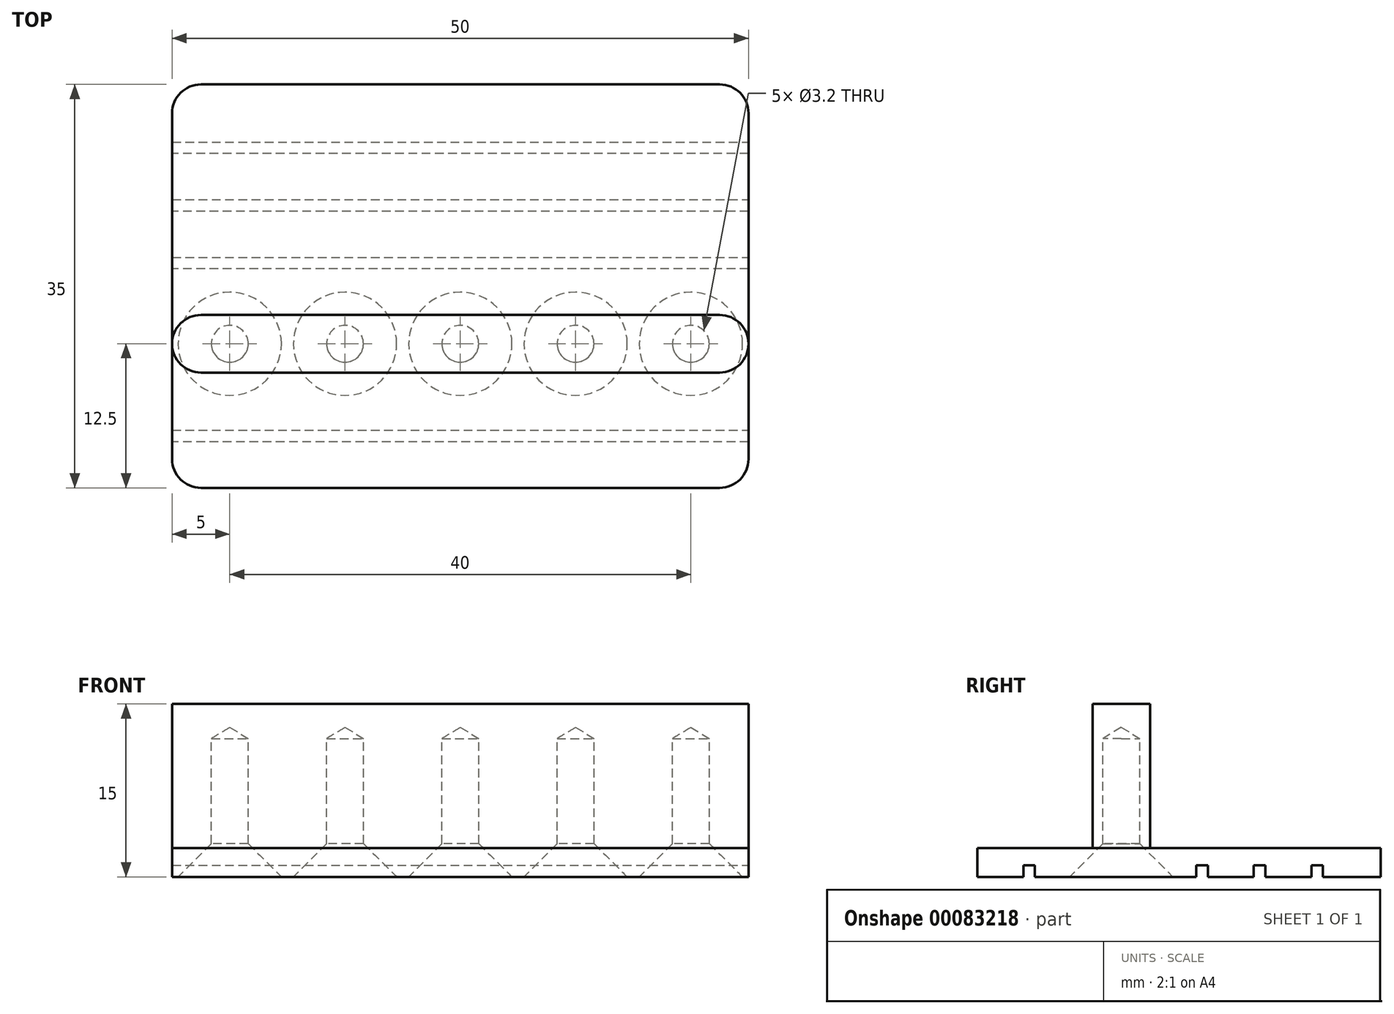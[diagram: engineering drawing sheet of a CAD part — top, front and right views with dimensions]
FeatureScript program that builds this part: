
annotation { "Feature Type Name" : "Feature", "Feature Type Description" : "" }
export const myFeature = defineFeature(function(context is Context, id is Id, definition is map)
    precondition{}
    {
        {
            var Q0;
            Q0=qCreatedBy(makeId("Top.planeOp"),FACE);
            var sketch = newSketch(context, id + "F0", { "sketchPlane" : qUnion([Q0])});
            skLineSegment(sketch, "E0.bottom", {"start": v(25, 17.5) * mm, "end": v(-25, 17.5) * mm});
            skLineSegment(sketch, "E0.top", {"start": v(25, -17.5) * mm, "end": v(-25, -17.5) * mm});
            skLineSegment(sketch, "E0.left", {"start": v(25, 17.5) * mm, "end": v(25, -17.5) * mm});
            skLineSegment(sketch, "E0.right", {"start": v(-25, 17.5) * mm, "end": v(-25, -17.5) * mm});
            skPoint(sketch, "E0.middle", {"position": v(0, 0) * mm});
            skLineSegment(sketch, "E1", {"start": v(-25, -7.5) * mm, "end": v(25, -7.5) * mm});
            skLineSegment(sketch, "E2", {"start": v(25, -7.5) * mm, "end": v(25, -2.5) * mm});
            skLineSegment(sketch, "E3", {"start": v(25, -2.5) * mm, "end": v(-25, -2.5) * mm});
            skLineSegment(sketch, "E4", {"start": v(-25, -5) * mm, "end": v(25, -5) * mm, "construction": true});
            skPoint(sketch, "E5", {"position": v(0, -5) * mm});
            skPoint(sketch, "E6", {"position": v(20, -5) * mm});
            skPoint(sketch, "E7", {"position": v(-20, -5) * mm});
            skPoint(sketch, "E8", {"position": v(-10, -5) * mm});
            skPoint(sketch, "E9", {"position": v(10, -5) * mm});
            skLineSegment(sketch, "E10", {"start": v(-25, 12.5) * mm, "end": v(25, 12.5) * mm});
            skLineSegment(sketch, "E11", {"start": v(25, 12.5) * mm, "end": v(25, 11.5) * mm});
            skLineSegment(sketch, "E12", {"start": v(25, 11.5) * mm, "end": v(-25, 11.5) * mm});
            skLineSegment(sketch, "E13.0.1.0", {"start": v(25, 6.5) * mm, "end": v(-25, 6.5) * mm});
            skLineSegment(sketch, "E13.0.1.1", {"start": v(-25, 7.5) * mm, "end": v(25, 7.5) * mm});
            skLineSegment(sketch, "E13.0.2.0", {"start": v(25, 1.5) * mm, "end": v(-25, 1.5) * mm});
            skLineSegment(sketch, "E13.0.2.1", {"start": v(-25, 2.5) * mm, "end": v(25, 2.5) * mm});
            skLineSegment(sketch, "E13.0.3.0", {"start": v(25, -3.5) * mm, "end": v(-25, -3.5) * mm});
            skLineSegment(sketch, "E13.0.3.1", {"start": v(-25, -2.5) * mm, "end": v(25, -2.5) * mm});
            skLineSegment(sketch, "E13.0.4.0", {"start": v(25, -8.5) * mm, "end": v(-25, -8.5) * mm});
            skLineSegment(sketch, "E13.0.5.0", {"start": v(25, -13.5) * mm, "end": v(-25, -13.5) * mm});
            skLineSegment(sketch, "E13.0.5.1", {"start": v(-25, -12.5) * mm, "end": v(25, -12.5) * mm});
            skLineSegment(sketch, "E13.direction1", {"start": v(-25, 11.5) * mm, "end": v(0, 11.5) * mm, "construction": true});
            skLineSegment(sketch, "E13.direction2", {"start": v(-25, 11.5) * mm, "end": v(-25, 6.5) * mm, "construction": true});
            skSolve(sketch);
        }
        {
            var Q0;
            {var subQ0=sQuery(id+"F0.wireOp",EDGE,"E0.bottom");Q0=makeQuery(id+"F0.imprint","IMPRINT",FACE,{"disambiguationData":[TD([[makeQuery(id+"F0.imprint","IMPRINT",EDGE,{"derivedFrom":subQ0}),1.0]])]});}
            var Q1;
            {var subQ0=sQuery(id+"F0.wireOp",EDGE,"E1");Q1=makeQuery(id+"F0.imprint","IMPRINT",FACE,{"disambiguationData":[TD([[makeQuery(id+"F0.imprint","IMPRINT",EDGE,{"derivedFrom":subQ0}),1.0]])]});}
            var Q2;
            {var subQ0=sQuery(id+"F0.wireOp",EDGE,"E0.top");Q2=makeQuery(id+"F0.imprint","IMPRINT",FACE,{"disambiguationData":[TD([[makeQuery(id+"F0.imprint","IMPRINT",EDGE,{"derivedFrom":subQ0}),-1.0]])]});}
            var Q3;
            {var subQ0=sQuery(id+"F0.wireOp",EDGE,"E13.0.5.0");Q3=makeQuery(id+"F0.imprint","IMPRINT",FACE,{"disambiguationData":[TD([[makeQuery(id+"F0.imprint","IMPRINT",EDGE,{"derivedFrom":subQ0}),-1.0]])]});}
            var Q4;
            {var subQ0=sQuery(id+"F0.wireOp",EDGE,"E13.0.4.0");Q4=makeQuery(id+"F0.imprint","IMPRINT",FACE,{"disambiguationData":[TD([[makeQuery(id+"F0.imprint","IMPRINT",EDGE,{"derivedFrom":subQ0}),1.0]])]});}
            var Q5;
            {var subQ0=sQuery(id+"F0.wireOp",EDGE,"E1");Q5=makeQuery(id+"F0.imprint","IMPRINT",FACE,{"disambiguationData":[TD([[makeQuery(id+"F0.imprint","IMPRINT",EDGE,{"derivedFrom":subQ0}),1.0]])]});}
            var Q6;
            {var subQ0=sQuery(id+"F0.wireOp",EDGE,"E3");Q6=makeQuery(id+"F0.imprint","IMPRINT",FACE,{"disambiguationData":[TD([[makeQuery(id+"F0.imprint","IMPRINT",EDGE,{"derivedFrom":subQ0}),1.0]])]});}
            var Q7;
            {var subQ0=sQuery(id+"F0.wireOp",EDGE,"E3");Q7=makeQuery(id+"F0.imprint","IMPRINT",FACE,{"disambiguationData":[TD([[makeQuery(id+"F0.imprint","IMPRINT",EDGE,{"derivedFrom":subQ0}),-1.0]])]});}
            var Q8;
            {var subQ0=sQuery(id+"F0.wireOp",EDGE,"E13.0.1.0");Q8=makeQuery(id+"F0.imprint","IMPRINT",FACE,{"disambiguationData":[TD([[makeQuery(id+"F0.imprint","IMPRINT",EDGE,{"derivedFrom":subQ0}),-1.0]])]});}
            var Q9;
            {var subQ0=sQuery(id+"F0.wireOp",EDGE,"E12");Q9=makeQuery(id+"F0.imprint","IMPRINT",FACE,{"disambiguationData":[TD([[makeQuery(id+"F0.imprint","IMPRINT",EDGE,{"derivedFrom":subQ0}),1.0]])]});}
            var Q10;
            {var subQ0=sQuery(id+"F0.wireOp",EDGE,"E10");Q10=makeQuery(id+"F0.imprint","IMPRINT",FACE,{"disambiguationData":[TD([[makeQuery(id+"F0.imprint","IMPRINT",EDGE,{"derivedFrom":subQ0}),-1.0]])]});}
            var Q11;
            {var subQ0=sQuery(id+"F0.wireOp",EDGE,"E1");Q11=makeQuery(id+"F0.imprint","IMPRINT",FACE,{"disambiguationData":[TD([[makeQuery(id+"F0.imprint","IMPRINT",EDGE,{"derivedFrom":subQ0}),-1.0]])]});}
            var Q12;
            {var subQ0=sQuery(id+"F0.wireOp",EDGE,"E13.0.2.0");Q12=makeQuery(id+"F0.imprint","IMPRINT",FACE,{"disambiguationData":[TD([[makeQuery(id+"F0.imprint","IMPRINT",EDGE,{"derivedFrom":subQ0}),-1.0]])]});}
            var Q13;
            {var subQ0=sQuery(id+"F0.wireOp",EDGE,"E13.0.1.0");Q13=makeQuery(id+"F0.imprint","IMPRINT",FACE,{"disambiguationData":[TD([[makeQuery(id+"F0.imprint","IMPRINT",EDGE,{"derivedFrom":subQ0}),1.0]])]});}
            extrude(context, id + "F1", {"entities" : qUnion([Q0, Q1, Q2, Q3, Q4, Q5, Q6, Q7, Q8, Q9, Q10, Q11, Q12, Q13]), "depth" : 2.5 * mm});
        }
        {
            var Q0;
            {var subQ0=sQuery(id+"F0.wireOp",EDGE,"E1");Q0=makeQuery(id+"F0.imprint","IMPRINT",FACE,{"disambiguationData":[TD([[makeQuery(id+"F0.imprint","IMPRINT",EDGE,{"derivedFrom":subQ0}),1.0]])]});}
            var Q1;
            {var subQ0=sQuery(id+"F0.wireOp",EDGE,"E3");Q1=makeQuery(id+"F0.imprint","IMPRINT",FACE,{"disambiguationData":[TD([[makeQuery(id+"F0.imprint","IMPRINT",EDGE,{"derivedFrom":subQ0}),1.0]])]});}
            extrude(context, id + "F2", {"entities" : qUnion([Q0, Q1]), "operationType" : NewBodyOperationType.ADD, "depth" : 15 * mm});
        }
        {
            var Q0;
            Q0=makeQuery(id+"F1.opExtrude","SWEPT_EDGE",EDGE,{"disambiguationData":[OSD([sQuery(id+"F0.wireOp",EDGE,"E0.bottom"),sQuery(id+"F0.wireOp",EDGE,"E0.right")])]});
            var Q1;
            Q1=makeQuery(id+"F1.opExtrude","SWEPT_EDGE",EDGE,{"disambiguationData":[OSD([sQuery(id+"F0.wireOp",EDGE,"E0.bottom"),sQuery(id+"F0.wireOp",EDGE,"E0.left")])]});
            var Q2;
            {var subQ0=sQuery(id+"F0.wireOp",EDGE,"E0.left");Q2=qUnion([makeQuery(id+"F2.opExtrude","SWEPT_EDGE",EDGE,{"disambiguationData":[OSD([subQ0,sQuery(id+"F0.wireOp",EDGE,"E3")])]}),makeQuery(id+"F2.opExtrude","SWEPT_EDGE",EDGE,{"disambiguationData":[OSD([subQ0,sQuery(id+"F0.wireOp",EDGE,"E1")])]})]);}
            var Q3;
            {var subQ0=sQuery(id+"F0.wireOp",EDGE,"E0.right");Q3=qUnion([makeQuery(id+"F2.opExtrude","SWEPT_EDGE",EDGE,{"disambiguationData":[OSD([subQ0,sQuery(id+"F0.wireOp",EDGE,"E3")])]}),makeQuery(id+"F2.opExtrude","SWEPT_EDGE",EDGE,{"disambiguationData":[OSD([subQ0,sQuery(id+"F0.wireOp",EDGE,"E1")])]})]);}
            var Q4;
            Q4=makeQuery(id+"F1.opExtrude","SWEPT_EDGE",EDGE,{"disambiguationData":[OSD([sQuery(id+"F0.wireOp",EDGE,"E0.top"),sQuery(id+"F0.wireOp",EDGE,"E0.right")])]});
            var Q5;
            Q5=makeQuery(id+"F1.opExtrude","SWEPT_EDGE",EDGE,{"disambiguationData":[OSD([sQuery(id+"F0.wireOp",EDGE,"E0.top"),sQuery(id+"F0.wireOp",EDGE,"E0.left")])]});
            var Q6;
            {var subQ0=sQuery(id+"F0.wireOp",EDGE,"E0.left");Q6=qUnion([makeQuery(id+"F2.opExtrude","SWEPT_EDGE",EDGE,{"disambiguationData":[OSD([subQ0,sQuery(id+"F0.wireOp",EDGE,"E3")])]}),makeQuery(id+"F2.opExtrude","SWEPT_EDGE",EDGE,{"disambiguationData":[OSD([subQ0,sQuery(id+"F0.wireOp",EDGE,"E1")])]})]);}
            var Q7;
            {var subQ0=sQuery(id+"F0.wireOp",EDGE,"E0.right");Q7=qUnion([makeQuery(id+"F2.opExtrude","SWEPT_EDGE",EDGE,{"disambiguationData":[OSD([subQ0,sQuery(id+"F0.wireOp",EDGE,"E3")])]}),makeQuery(id+"F2.opExtrude","SWEPT_EDGE",EDGE,{"disambiguationData":[OSD([subQ0,sQuery(id+"F0.wireOp",EDGE,"E1")])]})]);}
            fillet(context, id + "F3", {"entities" : qUnion([Q0, Q1, Q2, Q3, Q4, Q5, Q6, Q7]), "radius" : 2.5 * mm, "tangentPropagation" : true, "allowEdgeOverflow" : false});
        }
        {
            var Q0;
            Q0=sQuery(id+"F0.wireOp",VERTEX,"E6");
            var Q1;
            Q1=sQuery(id+"F0.wireOp",VERTEX,"E9");
            var Q2;
            Q2=sQuery(id+"F0.wireOp",VERTEX,"E5");
            var Q3;
            Q3=sQuery(id+"F0.wireOp",VERTEX,"E8");
            var Q4;
            Q4=sQuery(id+"F0.wireOp",VERTEX,"E7");
            var Q5;
            Q5=makeQuery(id+"F1.opExtrude","SWEPT_BODY",BODY,{"disambiguationData":[OSD([sQuery(id+"F0.wireOp",EDGE,"E0.bottom"),sQuery(id+"F0.wireOp",EDGE,"E0.top"),sQuery(id+"F0.wireOp",EDGE,"E0.left"),sQuery(id+"F0.wireOp",EDGE,"E0.right")])]});
            hole(context, id + "F4", {"style" : HoleStyle.C_SINK, "endStyle" : HoleEndStyle.BLIND, "oppositeDirection" : true, "standardTappedOrClearance" : lookupTablePath({ "standard" : "ISO", "engagement" : "75%", "pitch" : "0.75 mm", "size" : "M4", "type" : "Tapped" }), "standardBlindInLast" : lookupTablePath({ "standard" : "ISO", "engagement" : "75%", "pitch" : "0.75 mm", "size" : "M4", "type" : "Tapped" }), "holeDiameter" : 3.2 * mm, "cSinkDiameter" : 8.96 * mm, "cSinkAngle" : 90 * degree, "holeDepth" : 12 * mm, "locations" : qUnion([Q0, Q1, Q2, Q3, Q4]), "scope" : qUnion([Q5]), "startStyle" : HoleStartStyle.PART});
        }
        {
            var Q0;
            {var subQ0=sQuery(id+"F0.wireOp",EDGE,"E13.0.5.0");Q0=makeQuery(id+"F0.imprint","IMPRINT",FACE,{"disambiguationData":[TD([[makeQuery(id+"F0.imprint","IMPRINT",EDGE,{"derivedFrom":subQ0}),-1.0]])]});}
            var Q1;
            {var subQ0=sQuery(id+"F0.wireOp",EDGE,"E13.0.2.0");Q1=makeQuery(id+"F0.imprint","IMPRINT",FACE,{"disambiguationData":[TD([[makeQuery(id+"F0.imprint","IMPRINT",EDGE,{"derivedFrom":subQ0}),-1.0]])]});}
            var Q2;
            {var subQ0=sQuery(id+"F0.wireOp",EDGE,"E13.0.1.0");Q2=makeQuery(id+"F0.imprint","IMPRINT",FACE,{"disambiguationData":[TD([[makeQuery(id+"F0.imprint","IMPRINT",EDGE,{"derivedFrom":subQ0}),-1.0]])]});}
            var Q3;
            {var subQ0=sQuery(id+"F0.wireOp",EDGE,"E10");Q3=makeQuery(id+"F0.imprint","IMPRINT",FACE,{"disambiguationData":[TD([[makeQuery(id+"F0.imprint","IMPRINT",EDGE,{"derivedFrom":subQ0}),-1.0]])]});}
            extrude(context, id + "F5", {"entities" : qUnion([Q0, Q1, Q2, Q3]), "operationType" : NewBodyOperationType.REMOVE, "depth" : 1 * mm});
        }
    });
